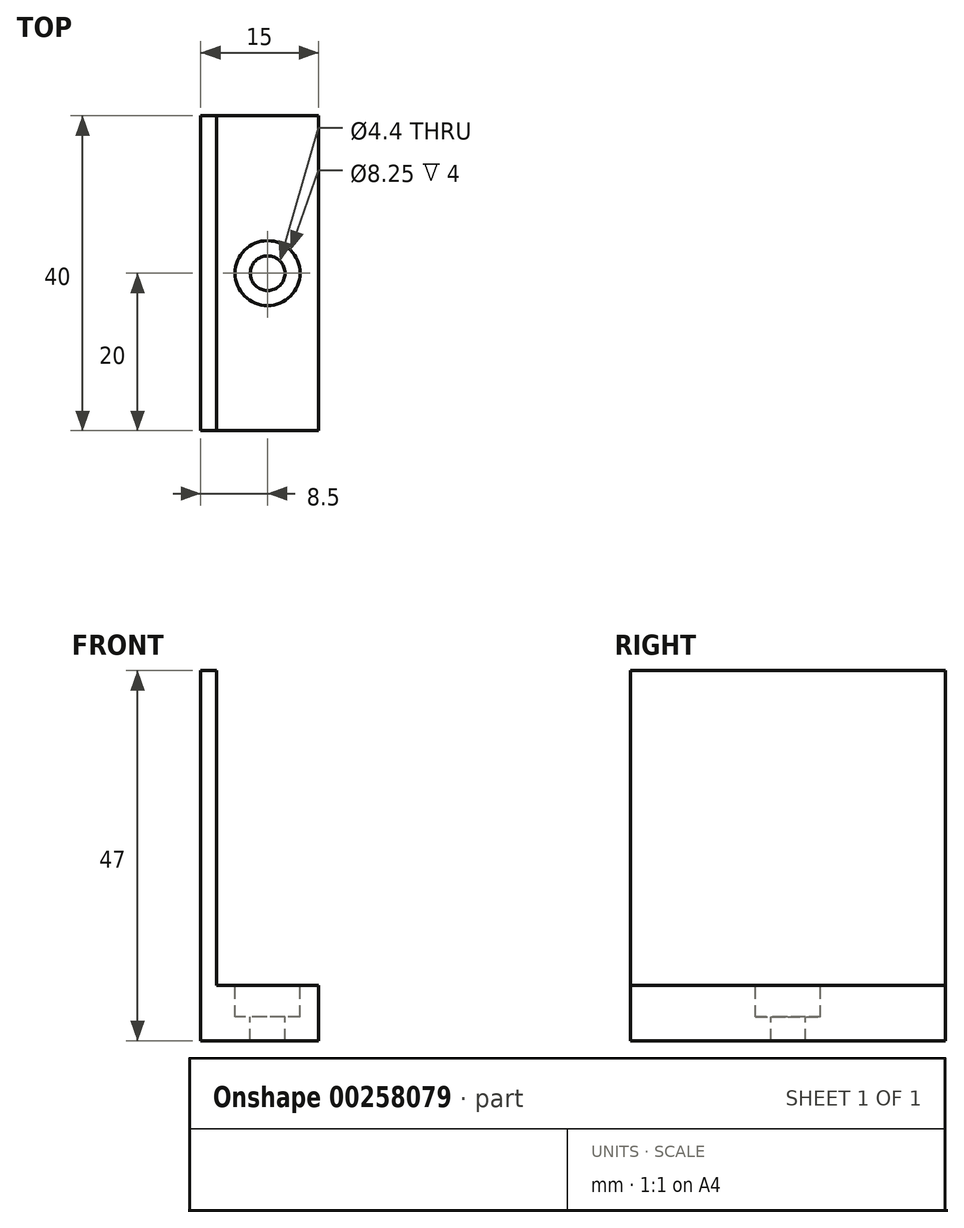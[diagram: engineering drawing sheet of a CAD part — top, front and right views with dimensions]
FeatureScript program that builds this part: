
annotation { "Feature Type Name" : "Feature", "Feature Type Description" : "" }
export const myFeature = defineFeature(function(context is Context, id is Id, definition is map)
    precondition{}
    {
        {
            var Q0;
            Q0=qCreatedBy(makeId("Top.planeOp"),FACE);
            var sketch = newSketch(context, id + "F0", { "sketchPlane" : qUnion([Q0])});
            skLineSegment(sketch, "E0.bottom", {"start": v(-7.5, 20) * mm, "end": v(7.5, 20) * mm});
            skLineSegment(sketch, "E0.top", {"start": v(-7.5, -20) * mm, "end": v(7.5, -20) * mm});
            skLineSegment(sketch, "E0.left", {"start": v(-7.5, 20) * mm, "end": v(-7.5, -20) * mm});
            skLineSegment(sketch, "E0.right", {"start": v(7.5, 20) * mm, "end": v(7.5, -20) * mm});
            skLineSegment(sketch, "E1", {"start": v(0, 20) * mm, "end": v(0, -20) * mm, "construction": true});
            skSolve(sketch);
        }
        {
            var Q0;
            Q0=makeQuery(id+"F0.imprint","IMPRINT",FACE,{"disambiguationData":[TD([[makeQuery(id+"F0.imprint","IMPRINT",EDGE,{"derivedFrom":sQuery(id+"F0.wireOp",EDGE,"E0.bottom")}),-1.0]])]});
            extrude(context, id + "F1", {"entities" : qUnion([Q0]), "depth" : 7 * mm});
        }
        {
            var Q0;
            Q0=makeQuery(id+"F1.opExtrude","CAP_FACE",FACE,{"disambiguationData":[OSD([sQuery(id+"F0.wireOp",EDGE,"E0.bottom"),sQuery(id+"F0.wireOp",EDGE,"E0.top"),sQuery(id+"F0.wireOp",EDGE,"E0.left"),sQuery(id+"F0.wireOp",EDGE,"E0.right")])],"isStart":false});
            var sketch = newSketch(context, id + "F2", { "sketchPlane" : qUnion([Q0])});
            skLineSegment(sketch, "E2.bottom", {"start": v(-7.5, 20) * mm, "end": v(-5.5, 20) * mm});
            skLineSegment(sketch, "E2.top", {"start": v(-7.5, -20) * mm, "end": v(-5.5, -20) * mm});
            skLineSegment(sketch, "E2.left", {"start": v(-7.5, 20) * mm, "end": v(-7.5, -20) * mm});
            skLineSegment(sketch, "E2.right", {"start": v(-5.5, 20) * mm, "end": v(-5.5, -20) * mm});
            skSolve(sketch);
        }
        {
            var Q0;
            Q0=makeQuery(id+"F2.imprint","IMPRINT",FACE,{"disambiguationData":[TD([[makeQuery(id+"F2.imprint","IMPRINT",EDGE,{"derivedFrom":sQuery(id+"F2.wireOp",EDGE,"E2.bottom")}),-1.0]])]});
            extrude(context, id + "F3", {"entities" : qUnion([Q0]), "operationType" : NewBodyOperationType.ADD, "depth" : 40 * mm});
        }
        {
            var Q0;
            Q0=makeQuery(id+"F1.opExtrude","CAP_FACE",FACE,{"disambiguationData":[OSD([sQuery(id+"F0.wireOp",EDGE,"E0.bottom"),sQuery(id+"F0.wireOp",EDGE,"E0.top"),sQuery(id+"F0.wireOp",EDGE,"E0.left"),sQuery(id+"F0.wireOp",EDGE,"E0.right")])],"isStart":false});
            var sketch = newSketch(context, id + "F4", { "sketchPlane" : qUnion([Q0])});
            skLineSegment(sketch, "E3", {"start": v(-5.5, 0) * mm, "end": v(7.5, 0) * mm, "construction": true});
            skPoint(sketch, "E4", {"position": v(1, 0) * mm});
            skSolve(sketch);
        }
        {
            var Q0;
            Q0=sQuery(id+"F4.wireOp",VERTEX,"E4");
            var Q1;
            Q1=makeQuery(id+"F1.opExtrude","SWEPT_BODY",BODY,{"disambiguationData":[OSD([sQuery(id+"F0.wireOp",EDGE,"E0.bottom"),sQuery(id+"F0.wireOp",EDGE,"E0.top"),sQuery(id+"F0.wireOp",EDGE,"E0.left"),sQuery(id+"F0.wireOp",EDGE,"E0.right")])]});
            hole(context, id + "F5", {"style" : HoleStyle.C_BORE, "endStyle" : HoleEndStyle.THROUGH, "standardTappedOrClearance" : lookupTablePath({ "standard" : "ISO", "fit" : "Normal", "size" : "M4", "type" : "Clearance" }), "standardBlindInLast" : lookupTablePath({ "fit" : "Standard", "standard" : "ISO", "size" : "M4", "type" : "Clearance" }), "holeDiameter" : 4.4 * mm, "cBoreDiameter" : 8.25 * mm, "cBoreDepth" : 4 * mm, "tappedDepth" : 12 * mm, "tapClearance" : 3, "locations" : qUnion([Q0]), "scope" : qUnion([Q1])});
        }
    });
